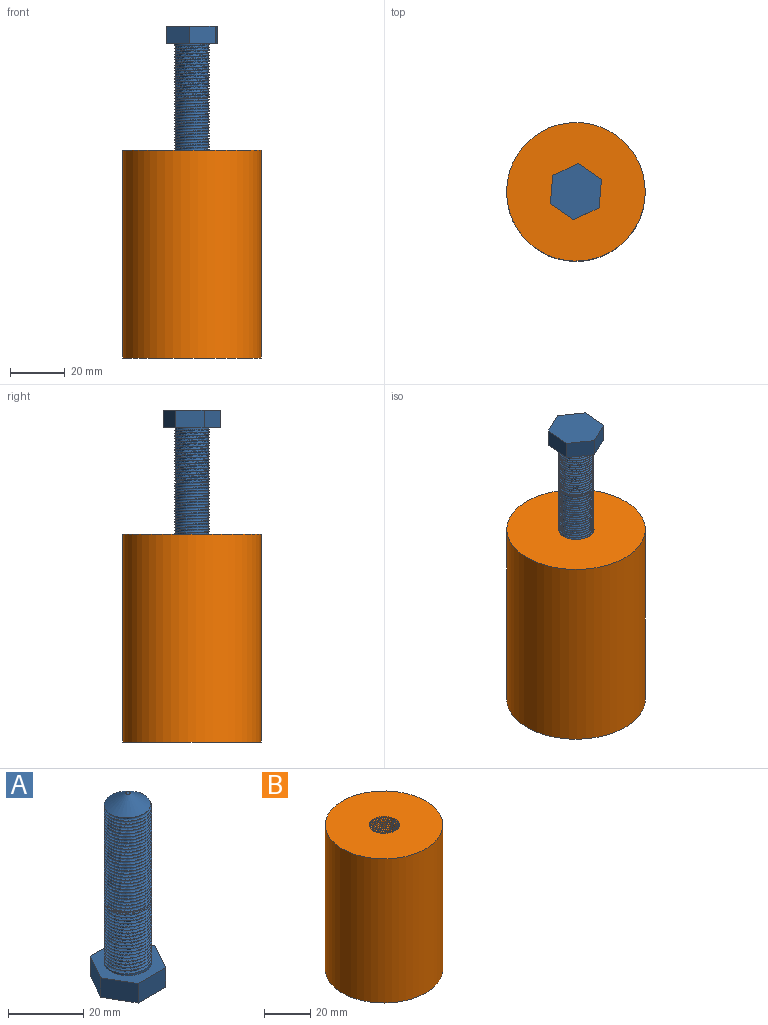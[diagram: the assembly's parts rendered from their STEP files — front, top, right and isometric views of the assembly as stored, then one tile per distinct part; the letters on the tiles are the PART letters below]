
ASSEMBLY  parts=2 mates=1
PART A: 66 faces, bbox 20.7x17.9x61.5 mm
  f0: cone r=6.35mm half-angle=56.3deg, axis (0,0,-1), area 146.2mm2, adj f1,f63,f64,f65
  f1: bspline ~32.47x16.91mm, area 1767.6mm2, adj f0,f2,f3,f4,f5,f6,f7,f8
  f2: cylinder r=6.35mm len=12.7mm, axis (0,0,-1), area 1.7mm2, adj f1,f3,f63
  f3: cylinder r=6.35mm len=12.7mm, axis (0,0,-1), area 1.7mm2, adj f1,f2,f4
  f4: cylinder r=6.35mm len=12.7mm, axis (0,0,-1), area 1.7mm2, adj f1,f3,f5
  f5: cylinder r=6.35mm len=12.7mm, axis (0,0,-1), area 1.7mm2, adj f1,f4,f6
  f6: cylinder r=6.35mm len=12.7mm, axis (0,0,-1), area 1.7mm2, adj f1,f5,f7
  f7: cylinder r=6.35mm len=12.7mm, axis (0,0,-1), area 1.7mm2, adj f1,f6,f8
  f8: cylinder r=6.35mm len=12.7mm, axis (0,0,-1), area 1.7mm2, adj f1,f7,f9
  f9: cylinder r=6.35mm len=12.7mm, axis (0,0,-1), area 1.7mm2, adj f1,f8,f10
  f10: cylinder r=6.35mm len=12.7mm, axis (0,0,-1), area 1.7mm2, adj f1,f9,f11
  f11: cylinder r=6.35mm len=12.7mm, axis (0,0,-1), area 1.7mm2, adj f1,f10,f12
  f12: cylinder r=6.35mm len=12.7mm, axis (0,0,-1), area 1.7mm2, adj f1,f11,f13
  f13: cylinder r=6.35mm len=12.7mm, axis (0,0,-1), area 1.7mm2, adj f1,f12,f14
  f14: cylinder r=6.35mm len=12.7mm, axis (0,0,-1), area 1.7mm2, adj f1,f13,f15
  f15: cylinder r=6.35mm len=12.7mm, axis (0,0,-1), area 1.7mm2, adj f1,f14,f16
  f16: cylinder r=6.35mm len=12.7mm, axis (0,0,-1), area 1.7mm2, adj f1,f15,f17
  f17: cylinder r=6.35mm len=12.7mm, axis (0,0,-1), area 1.7mm2, adj f1,f16,f18
  f18: cylinder r=6.35mm len=12.7mm, axis (0,0,-1), area 1.7mm2, adj f1,f17,f19
  f19: cylinder r=6.35mm len=12.7mm, axis (0,0,-1), area 1.7mm2, adj f1,f18,f20
  f20: cylinder r=6.35mm len=12.7mm, axis (0,0,-1), area 1.7mm2, adj f1,f19,f21
  f21: cylinder r=6.35mm len=12.7mm, axis (0,0,-1), area 1.7mm2, adj f1,f20,f22
  f22: cylinder r=6.35mm len=12.7mm, axis (0,0,-1), area 1.7mm2, adj f1,f21,f23
  f23: cylinder r=6.35mm len=12.7mm, axis (0,0,-1), area 1.7mm2, adj f1,f22,f24
  f24: cylinder r=6.35mm len=12.7mm, axis (0,0,-1), area 1.7mm2, adj f1,f23,f25
  f25: cylinder r=6.35mm len=12.7mm, axis (0,0,-1), area 1.7mm2, adj f1,f24,f26
  f26: cylinder r=6.35mm len=12.7mm, axis (0,0,-1), area 1.7mm2, adj f1,f25,f27
  f27: cylinder r=6.35mm len=12.7mm, axis (0,0,-1), area 1.7mm2, adj f1,f26,f28
  f28: cylinder r=6.35mm len=12.7mm, axis (0,0,-1), area 1.7mm2, adj f1,f27,f29
  f29: cylinder r=6.35mm len=12.7mm, axis (0,0,-1), area 1.7mm2, adj f1,f28,f30
  f30: cylinder r=6.35mm len=12.7mm, axis (0,0,-1), area 1.7mm2, adj f1,f29,f31
  f31: cylinder r=6.35mm len=12.7mm, axis (0,0,-1), area 1.7mm2, adj f1,f30,f32
  f32: cylinder r=6.35mm len=12.7mm, axis (0,0,-1), area 1.7mm2, adj f1,f31,f33,f34,f62
  f33: bspline ~16.91x14.65mm, area 0mm2, adj f32
  f34: cylinder r=6.35mm len=12.7mm, axis (0,0,-1), area 1.7mm2, adj f32,f35,f62
  f35: cylinder r=6.35mm len=12.7mm, axis (0,0,-1), area 1.7mm2, adj f34,f36,f62
  f36: cylinder r=6.35mm len=12.7mm, axis (0,0,-1), area 1.7mm2, adj f35,f37,f62
  f37: cylinder r=6.35mm len=12.7mm, axis (0,0,-1), area 1.7mm2, adj f36,f38,f62
  f38: cylinder r=6.35mm len=12.7mm, axis (0,0,-1), area 1.7mm2, adj f37,f39,f62
  f39: cylinder r=6.35mm len=12.7mm, axis (0,0,-1), area 1.7mm2, adj f38,f40,f62
  f40: cylinder r=6.35mm len=12.7mm, axis (0,0,-1), area 1.7mm2, adj f39,f41,f62
  f41: cylinder r=6.35mm len=12.7mm, axis (0,0,-1), area 1.7mm2, adj f40,f42,f62
  f42: cylinder r=6.35mm len=12.7mm, axis (0,0,-1), area 1.7mm2, adj f41,f43,f62
  f43: cylinder r=6.35mm len=12.7mm, axis (0,0,-1), area 1.7mm2, adj f42,f44,f62
  f44: cylinder r=6.35mm len=12.7mm, axis (0,0,-1), area 1.7mm2, adj f43,f45,f62
  f45: cylinder r=6.35mm len=12.7mm, axis (0,0,-1), area 1.7mm2, adj f44,f46,f62
  f46: cylinder r=6.35mm len=12.7mm, axis (0,0,-1), area 1.7mm2, adj f45,f47,f62
  f47: cylinder r=6.35mm len=12.7mm, axis (0,0,-1), area 1.7mm2, adj f46,f48,f62
  f48: cylinder r=6.35mm len=12.7mm, axis (0,0,-1), area 1.7mm2, adj f47,f49,f62
  f49: cylinder r=6.35mm len=12.7mm, axis (0,0,-1), area 1.7mm2, adj f48,f50,f62
  f50: cylinder r=6.35mm len=12.7mm, axis (0,0,-1), area 1.7mm2, adj f49,f51,f62
  f51: cylinder r=6.35mm len=12.7mm, axis (0,0,-1), area 1.7mm2, adj f50,f52,f62
  f52: cylinder r=6.35mm len=12.7mm, axis (0,0,-1), area 21.1mm2, adj f51,f53,f61,f62
  f53: plane 20.7x17.93mm, normal (0,0,-1), area 151.6mm2, adj f52,f54,f56,f57,f58,f59,f60
  f54: plane 8.96x6.35mm, normal (0.87,-0.5,0), area 65.7mm2, adj f53,f55,f56,f60
  f55: plane 20.7x17.93mm, normal (0,0,1), area 278.3mm2, adj f54,f56,f57,f58,f59,f60
  f56: plane 10.35x6.35mm, normal (0,-1,0), area 65.7mm2, adj f53,f54,f55,f57
  f57: plane 8.96x6.35mm, normal (-0.87,-0.5,0), area 65.7mm2, adj f53,f55,f56,f58
  f58: plane 8.96x6.35mm, normal (-0.87,0.5,0), area 65.7mm2, adj f53,f55,f57,f59
  f59: plane 10.35x6.35mm, normal (0,1,0), area 65.7mm2, adj f53,f55,f58,f60
  f60: plane 8.96x6.35mm, normal (0.87,0.5,0), area 65.7mm2, adj f53,f54,f55,f59
  f61: plane 0.97x0.49mm, normal (0,-1,0), area 0.4mm2, adj f52,f62
  f62: bspline ~21.29x16.91mm, area 1116.1mm2, adj f32,f34,f35,f36,f37,f38,f39,f40
  f63: cylinder r=6.35mm len=12.7mm, axis (0,0,-1), area 5.5mm2, adj f0,f1,f2,f64
  f64: plane 0.76x0.49mm, normal (0,-1,0), area 0.3mm2, adj f0,f1,f63
  f65: plane 1.27x1.27mm, normal (0,0,1), area 1.3mm2, adj f0
PART B: 8 faces, bbox 51x51x76.7 mm
  f0: plane 51.04x51.04mm, normal (0,0,1), area 1898.4mm2, adj f1,f3,f5,f7
  f1: cylinder r=25.4mm len=76.2mm, axis (0,0,-1), area 12161mm2, adj f0,f2
  f2: plane 50.8x50.8mm, normal (0,0,-1), area 2026.8mm2, adj f1
  f3: cylinder r=6.35mm len=57.15mm, axis (0,0,-1), area 1067.4mm2, adj f0,f4,f5,f6,f7
  f4: plane 12.92x12.92mm, normal (0,0,1), area 124.9mm2, adj f3,f6,f7
  f5: plane 0.33x0.33mm, normal (0,-1,0), area 0.1mm2, adj f0,f3,f7
  f6: plane 0.58x0.58mm, normal (0,1,0), area 0.2mm2, adj f3,f4,f7
  f7: bspline ~57.66x13.2mm, area 1634.8mm2, adj f0,f3,f4,f5,f6
PLACE A rot(axis=(-0.3,-0.95,0),180deg) t=(-0.17,-0.15,115.02)mm
PLACE B t=(-0.17,-0.15,0.21)mm fixed
MATE cylindrical A.f0 <-> B.f1  axis (0,0,1) through (-0.17,-0.15,115.53)mm
